# Revit family: Rough_In_Valve-GROHE-29038001
name_source: partatom
category: Pipe Accessories
revit_build: Autodesk Revit 2014 (Build: 20130308_1515(x64)
units: mm (PartAtom-declared; Revit-internal decimal feet)

## types (1)
- 29038001
    Assembly Code = D2020
    CW Connection = Yes
    CWFU = 2
    Cold Water Connection Diameter = 1/2"
    Default Elevation = 0"
    Description = Rough-in set ½"
    HW Connection = Yes
    HWFU = 3
    Height = 4 7/16"
    Hot Water Connection Diameter = 1"
    Length = 5 15/16"
    Manufacturer = GROHE
    Material = Copper-Grohe-000-Brass
    Model = 29038001
    Price = Prices may vary. Please consult Manufacturer Representative for most up-to-date price list.
    Product Page URL = https://www.grohe.us
    Tempered Water Connection Diameter = 1/2"
    URL = https://www.grohe.us
    Vent Connection = No
    WFU = 4
    Warranty Information = Limited Lifetime Warranty
    Waste Connection = No
    Width = 5 15/16"

## geometry (parser evidence)
native form markers: Sweep x1
no freeform markers — native parametric forms only
